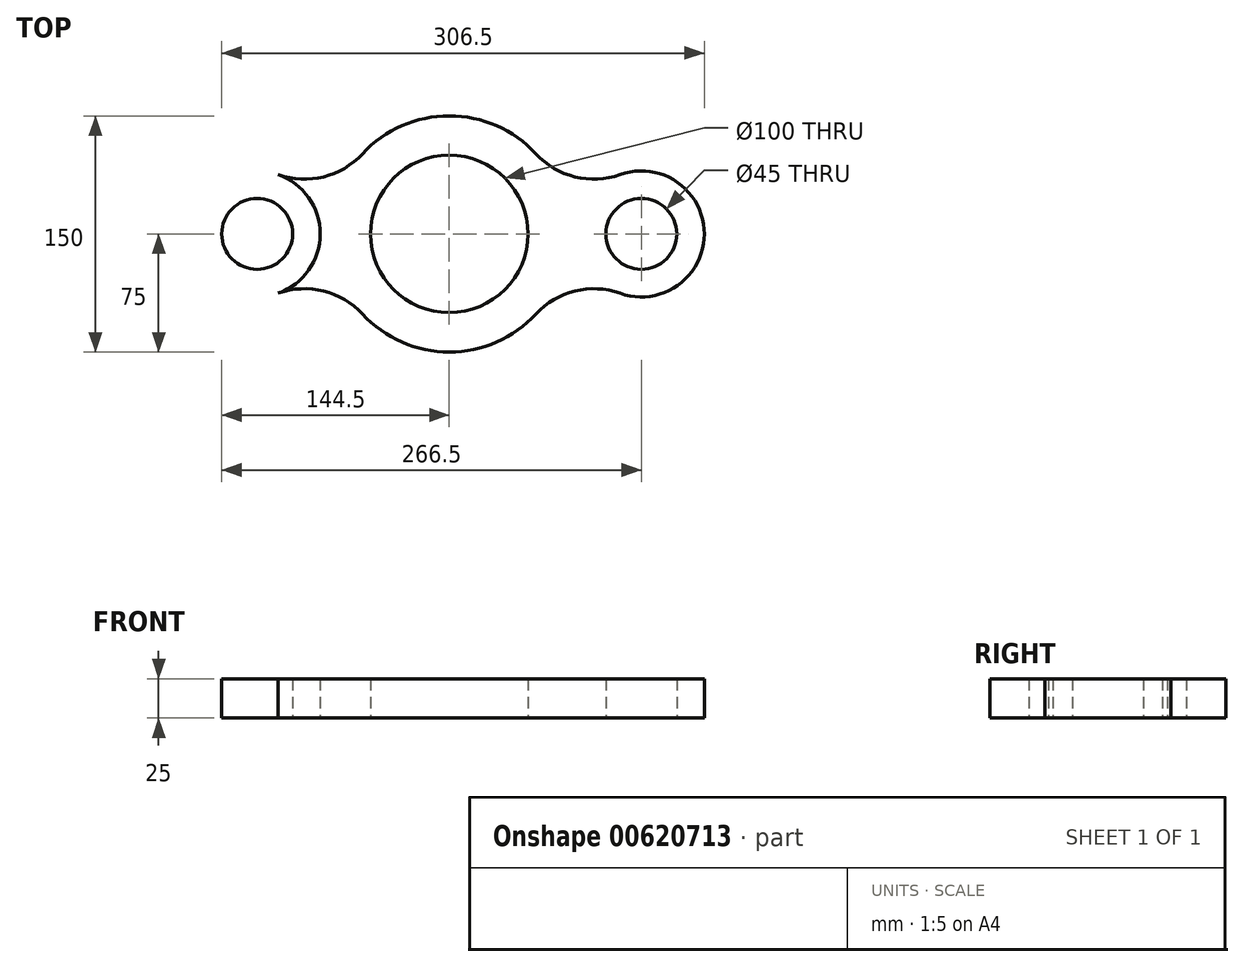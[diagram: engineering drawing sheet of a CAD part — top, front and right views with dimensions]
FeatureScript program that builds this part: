
annotation { "Feature Type Name" : "Feature", "Feature Type Description" : "" }
export const myFeature = defineFeature(function(context is Context, id is Id, definition is map)
    precondition{}
    {
        {
            var Q0;
            Q0=qCreatedBy(makeId("Top.planeOp"),FACE);
            var sketch = newSketch(context, id + "F0", { "sketchPlane" : qUnion([Q0])});
            skCircle(sketch, "E0", {"center": v(0, 0) * mm, "radius": 75 * mm});
            skCircle(sketch, "E1", {"center": v(122, 0) * mm, "radius": 40 * mm});
            skCircle(sketch, "E2", {"center": v(0, 0) * mm, "radius": 50 * mm});
            skCircle(sketch, "E3", {"center": v(122, 0) * mm, "radius": 22.5 * mm});
            skArc(sketch, "E4", {"start": v(55.1, 50.88) * mm, "mid": v(79.87, 36.25) * mm, "end": v(108.6, 37.69) * mm});
            skArc(sketch, "E5.MirrorCS", {"start": v(55.1, -50.88) * mm, "mid": v(79.87, -36.25) * mm, "end": v(108.6, -37.69) * mm});
            skArc(sketch, "E6.MirrorCS", {"start": v(-55.1, -50.88) * mm, "mid": v(-79.87, -36.25) * mm, "end": v(-108.6, -37.69) * mm});
            skArc(sketch, "E7.MirrorCS", {"start": v(-55.1, 50.88) * mm, "mid": v(-79.87, 36.25) * mm, "end": v(-108.6, 37.69) * mm});
            skCircle(sketch, "E8.MirrorC", {"center": v(-122, 0) * mm, "radius": 40 * mm});
            skCircle(sketch, "E9.MirrorC", {"center": v(-122, 0) * mm, "radius": 22.5 * mm});
            skSolve(sketch);
        }
        {
            var Q0;
            Q0=makeQuery(id+"F0.imprint","IMPRINT",FACE,{"disambiguationData":[TD([[makeQuery(id+"F0.imprint","IMPRINT",EDGE,{"derivedFrom":sQuery(id+"F0.wireOp",EDGE,"E2")}),-1.0]])]});
            var Q1;
            {var subQ0=sQuery(id+"F0.wireOp",EDGE,"E4");Q1=makeQuery(id+"F0.imprint","IMPRINT",FACE,{"disambiguationData":[TD([[makeQuery(id+"F0.imprint","IMPRINT",EDGE,{"derivedFrom":subQ0}),-1.0]])]});}
            var Q2;
            Q2=makeQuery(id+"F0.imprint","IMPRINT",FACE,{"disambiguationData":[TD([[makeQuery(id+"F0.imprint","IMPRINT",EDGE,{"derivedFrom":sQuery(id+"F0.wireOp",EDGE,"E3")}),-1.0]])]});
            var Q3;
            {var subQ0=sQuery(id+"F0.wireOp",EDGE,"E6.MirrorCS");Q3=makeQuery(id+"F0.imprint","IMPRINT",FACE,{"disambiguationData":[TD([[makeQuery(id+"F0.imprint","IMPRINT",EDGE,{"derivedFrom":subQ0}),-1.0]])]});}
            var Q4;
            Q4=makeQuery(id+"F0.imprint","IMPRINT",FACE,{"disambiguationData":[TD([[makeQuery(id+"F0.imprint","IMPRINT",EDGE,{"derivedFrom":sQuery(id+"F0.wireOp",EDGE,"E9.MirrorC")}),1.0]])]});
            extrude(context, id + "F1", {"entities" : qUnion([Q0, Q1, Q2, Q3, Q4]), "depth" : 25 * mm, "offsetDistance" : 25 * mm});
        }
    });
